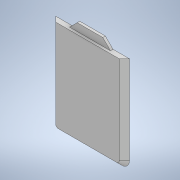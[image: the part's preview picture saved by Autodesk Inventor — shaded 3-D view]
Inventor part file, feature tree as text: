
AUTODESK INVENTOR PART (.ipt)
format: ipt  version: 2021.1 (Build 251245010, 245A)  size: 134,656 bytes
history: native  units: mm
features: extrude x2, sketch x2, chamfer x1, projected_geometry x1
ambient origin geometry x8: Origin, YZ Plane, XZ Plane, XY Plane, X Axis, Y Axis, Z Axis, Center Point
bodies: Volumenkörper1 (feature_tree)
feature tree (6):
  extrude  "Extrusion1"  Depth=2.0mm TaperAngle=45.0deg
  chamfer  "Fase1"  Distance=1.0mm
  extrude  "Extrusion2"  [1 undecoded]
  sketch  "Skizze1"  dims[d0=2.0mm d1=0.0mm d2=2.0mm d3=2.0mm d4=45.0deg d5=1.0mm d6=0.0mm]
  sketch  "Skizze2"
  projected_geometry  "Projizierte Kontur1"
note: 1 required parameter value undecoded (feature->parameter linkage not recoverable at this tier; creation-order binding heuristic only, values carry confidence <= 0.55)
